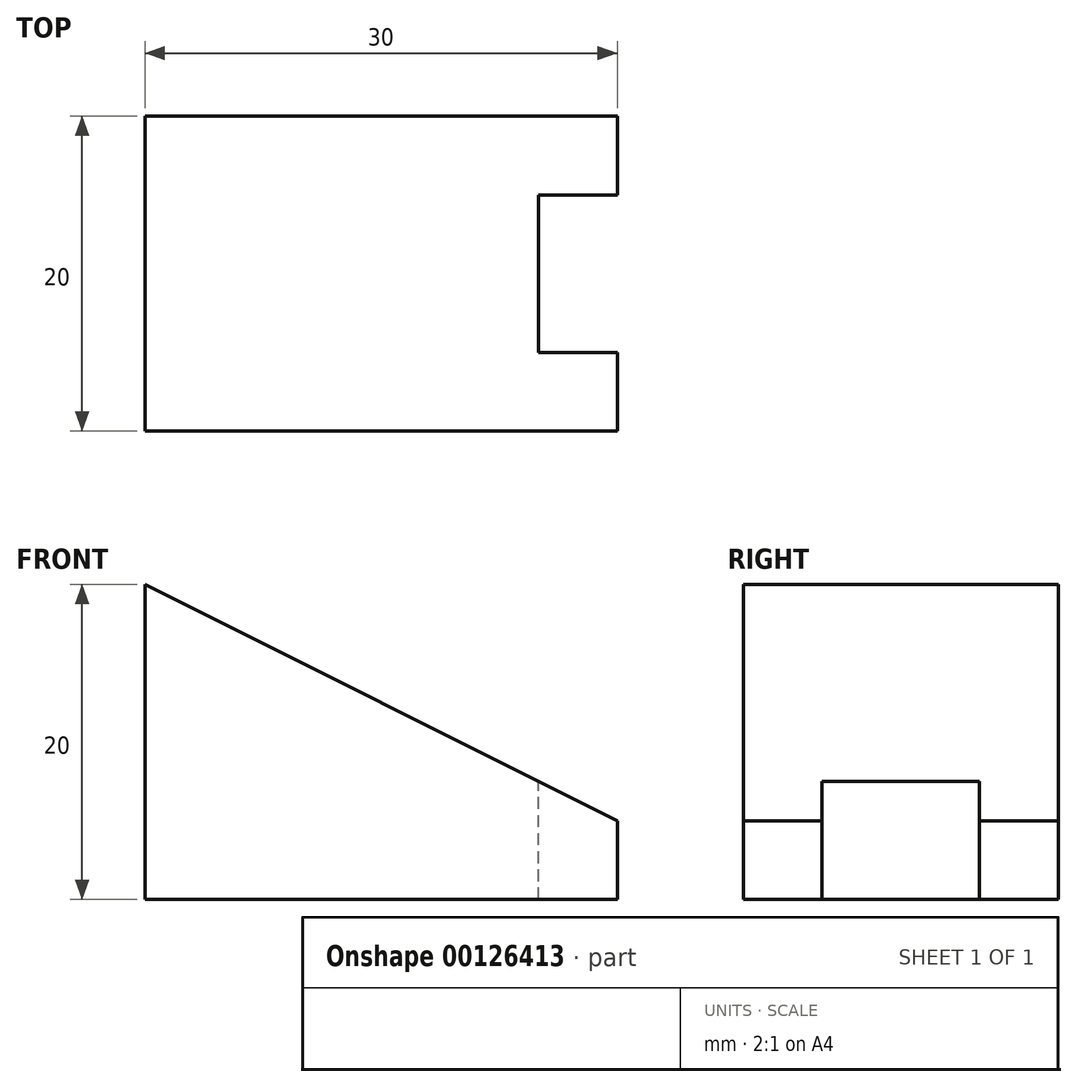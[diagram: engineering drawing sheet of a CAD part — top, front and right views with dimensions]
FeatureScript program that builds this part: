
annotation { "Feature Type Name" : "Feature", "Feature Type Description" : "" }
export const myFeature = defineFeature(function(context is Context, id is Id, definition is map)
    precondition{}
    {
        {
            var Q0;
            Q0=qCreatedBy(makeId("Front.planeOp"),FACE);
            var sketch = newSketch(context, id + "F0", { "sketchPlane" : qUnion([Q0])});
            skLineSegment(sketch, "E0", {"start": v(0, 0) * mm, "end": v(30, 0) * mm});
            skLineSegment(sketch, "E1", {"start": v(30, 0) * mm, "end": v(30, 5) * mm});
            skLineSegment(sketch, "E2", {"start": v(0, 0) * mm, "end": v(0, 20) * mm});
            skLineSegment(sketch, "E3", {"start": v(0, 20) * mm, "end": v(30, 5) * mm});
            skLineSegment(sketch, "E4", {"start": v(25, 5) * mm, "end": v(25, 7.5) * mm});
            skLineSegment(sketch, "E5", {"start": v(25, 5) * mm, "end": v(25, 0) * mm});
            skLineSegment(sketch, "E6", {"start": v(0, 20) * mm, "end": v(0, 10) * mm});
            skLineSegment(sketch, "E7", {"start": v(0, 10) * mm, "end": v(20, 10) * mm});
            skSolve(sketch);
        }
        {
            var Q0;
            Q0 = qSketchRegion(id + "F0", true);
            var Q1;
            Q1=makeQuery(id+"F0.imprint","IMPRINT",FACE,{"disambiguationData":[TD([[makeQuery(id+"F0.imprint","IMPRINT",EDGE,{"derivedFrom":sQuery(id+"F0.wireOp",EDGE,"E0")}),1.0]])]});
            extrude(context, id + "F1", {"entities" : qUnion([Q0, Q1]), "endBound" : BoundingType.SYMMETRIC, "depth" : 20 * mm});
        }
        {
            var Q0;
            {var subQ0=sQuery(id+"F0.wireOp",EDGE,"E6");Q0=makeQuery(id+"F0.imprint","IMPRINT",FACE,{"disambiguationData":[TD([[makeQuery(id+"F0.imprint","IMPRINT",EDGE,{"derivedFrom":subQ0}),1.0]])]});}
            var Q1;
            {var subQ2=sQuery(id+"F0.wireOp",EDGE,"E1");Q1=makeQuery(id+"F0.imprint","IMPRINT",FACE,{"disambiguationData":[TD([[makeQuery(id+"F0.imprint","IMPRINT",EDGE,{"derivedFrom":subQ2}),1.0]])]});}
            extrude(context, id + "F2", {"entities" : qUnion([Q0, Q1]), "operationType" : NewBodyOperationType.REMOVE, "endBound" : BoundingType.SYMMETRIC, "depth" : 10 * mm});
        }
    });
